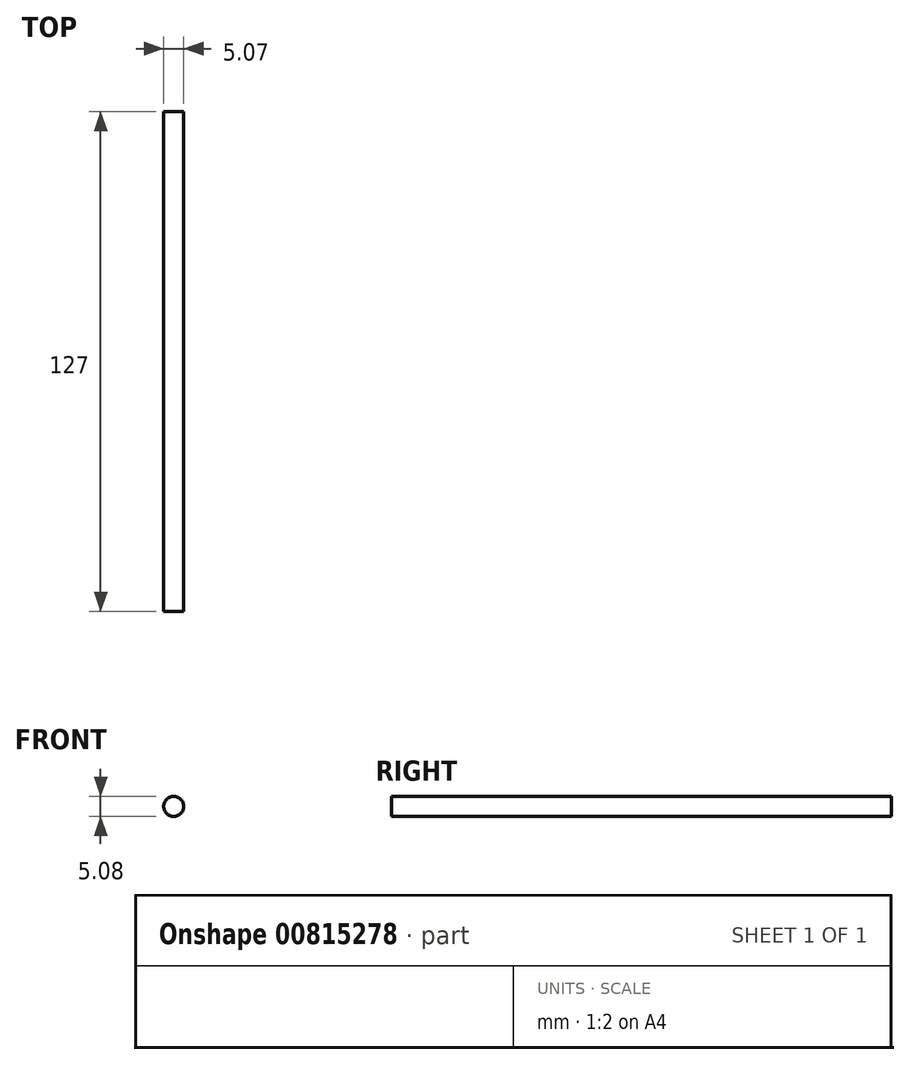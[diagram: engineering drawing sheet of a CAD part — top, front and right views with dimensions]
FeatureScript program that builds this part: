
annotation { "Feature Type Name" : "Feature", "Feature Type Description" : "" }
export const myFeature = defineFeature(function(context is Context, id is Id, definition is map)
    precondition{}
    {
        {
            var Q0;
            Q0=qCreatedBy(makeId("Front.planeOp"),FACE);
            var sketch = newSketch(context, id + "F0", { "sketchPlane" : qUnion([Q0])});
            skCircle(sketch, "E0", {"center": v(8.2, 9.66) * mm, "radius": 2.54 * mm});
            skSolve(sketch);
        }
        {
            var Q0;
            Q0 = qSketchRegion(id + "F0", true);
            extrude(context, id + "F1", {"entities" : qUnion([Q0]), "depth" : 127 * mm, "offsetDistance" : 25.4 * mm});
        }
    });
